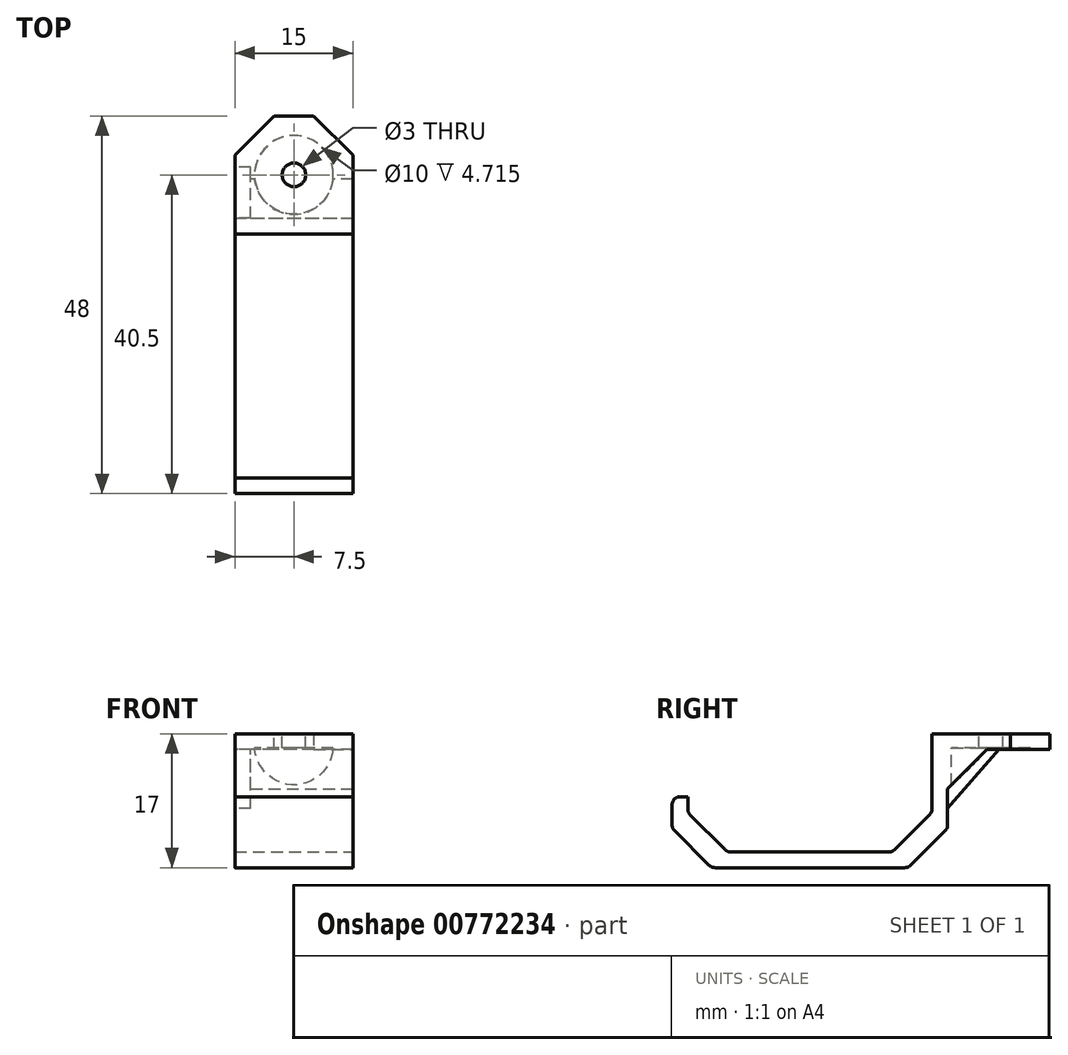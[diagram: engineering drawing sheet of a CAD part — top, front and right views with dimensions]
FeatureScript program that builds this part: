
annotation { "Feature Type Name" : "Feature", "Feature Type Description" : "" }
export const myFeature = defineFeature(function(context is Context, id is Id, definition is map)
    precondition{}
    {
        {
            var Q0;
            Q0=qCreatedBy(makeId("Right.planeOp"),FACE);
            var sketch = newSketch(context, id + "F0", { "sketchPlane" : qUnion([Q0])});
            skLineSegment(sketch, "E0", {"start": v(-35, 0) * mm, "end": v(0, 0) * mm});
            skLineSegment(sketch, "E1", {"start": v(0, 0) * mm, "end": v(0, 15) * mm});
            skLineSegment(sketch, "E2", {"start": v(0, 15) * mm, "end": v(13, 15) * mm});
            skLineSegment(sketch, "E3", {"start": v(13, 15) * mm, "end": v(13, 17) * mm});
            skLineSegment(sketch, "E4", {"start": v(13, 17) * mm, "end": v(-2, 17) * mm});
            skLineSegment(sketch, "E5", {"start": v(-2, 17) * mm, "end": v(-2, 2) * mm});
            skLineSegment(sketch, "E6", {"start": v(-2, 2) * mm, "end": v(-33, 2) * mm});
            skLineSegment(sketch, "E7", {"start": v(-33, 9) * mm, "end": v(-35, 9) * mm});
            skLineSegment(sketch, "E8", {"start": v(-35, 9) * mm, "end": v(-35, 0) * mm});
            skPoint(sketch, "E9", {"position": v(6.5, 15) * mm});
            skLineSegment(sketch, "E10", {"start": v(-33, 9) * mm, "end": v(-33, 2) * mm});
            skLineSegment(sketch, "E11", {"start": v(0, 7.5) * mm, "end": v(6.5, 15) * mm});
            skSolve(sketch);
        }
        {
            var Q0;
            {var subQ4=sQuery(id+"F0.wireOp",EDGE,"E0");Q0=makeQuery(id+"F0.imprint","IMPRINT",FACE,{"disambiguationData":[TD([[makeQuery(id+"F0.imprint","IMPRINT",EDGE,{"derivedFrom":subQ4}),1.0]])]});}
            extrude(context, id + "F1", {"entities" : qUnion([Q0]), "depth" : 15 * mm, "offsetDistance" : 25 * mm});
        }
        {
            var Q0;
            {var subQ3=sQuery(id+"F0.wireOp",EDGE,"E11");Q0=makeQuery(id+"F0.imprint","IMPRINT",FACE,{"disambiguationData":[TD([[makeQuery(id+"F0.imprint","IMPRINT",EDGE,{"derivedFrom":subQ3}),1.0]])]});}
            extrude(context, id + "F2", {"entities" : qUnion([Q0]), "operationType" : NewBodyOperationType.ADD, "depth" : 2 * mm, "offsetDistance" : 25 * mm});
        }
        {
            var Q0;
            Q0=makeQuery(id+"F1.opExtrude","SWEPT_FACE",FACE,{"disambiguationData":[OSD([sQuery(id+"F0.wireOp",EDGE,"E2")])]});
            var sketch = newSketch(context, id + "F3", { "sketchPlane" : qUnion([Q0])});
            skPoint(sketch, "E12", {"position": v(7.5, -5.5) * mm});
            skPoint(sketch, "E12.positionSnap0", {"position": v(0, -5.5) * mm});
            skPoint(sketch, "E12.positionSnap1", {"position": v(7.5, 2) * mm});
            skSolve(sketch);
        }
        {
            var Q0;
            Q0=sQuery(id+"F3.wireOp",VERTEX,"E12");
            var Q1;
            Q1=makeQuery(id+"F1.opExtrude","SWEPT_BODY",BODY,{"disambiguationData":[OSD([sQuery(id+"F0.wireOp",EDGE,"E0"),sQuery(id+"F0.wireOp",EDGE,"E1"),sQuery(id+"F0.wireOp",EDGE,"E2"),sQuery(id+"F0.wireOp",EDGE,"E3"),sQuery(id+"F0.wireOp",EDGE,"E4"),sQuery(id+"F0.wireOp",EDGE,"E5"),sQuery(id+"F0.wireOp",EDGE,"E6"),sQuery(id+"F0.wireOp",EDGE,"E7"),sQuery(id+"F0.wireOp",EDGE,"E8"),sQuery(id+"F0.wireOp",EDGE,"E10")])]});
            hole(context, id + "F4", {"style" : HoleStyle.C_BORE, "endStyle" : HoleEndStyle.BLIND, "holeDiameter" : 3 * mm, "cBoreDiameter" : 10 * mm, "cBoreDepth" : 0.2 * mm, "majorDiameter" : 5 * mm, "holeDepth" : 100 * mm, "isTappedThrough" : true, "tappedDepth" : 12 * mm, "tapClearance" : 3, "locations" : qUnion([Q0]), "scope" : qUnion([Q1]), "startStyle" : HoleStartStyle.PART});
        }
        {
            var Q0;
            Q0=makeQuery(id+"F1.opExtrude","SWEPT_EDGE",EDGE,{"disambiguationData":[OSD([sQuery(id+"F0.wireOp",EDGE,"E5"),sQuery(id+"F0.wireOp",EDGE,"E6")])]});
            var Q1;
            Q1=makeQuery(id+"F1.opExtrude","SWEPT_EDGE",EDGE,{"disambiguationData":[OSD([sQuery(id+"F0.wireOp",EDGE,"E6"),sQuery(id+"F0.wireOp",EDGE,"E10")])]});
            var Q2;
            Q2=makeQuery(id+"F1.opExtrude","SWEPT_EDGE",EDGE,{"disambiguationData":[OSD([sQuery(id+"F0.wireOp",EDGE,"E0"),sQuery(id+"F0.wireOp",EDGE,"E8")])]});
            var Q3;
            Q3=makeQuery(id+"F1.opExtrude","CAP_EDGE",EDGE,{"disambiguationData":[OSD([sQuery(id+"F0.wireOp",EDGE,"E3")])],"isStart":false});
            var Q4;
            Q4=makeQuery(id+"F1.opExtrude","CAP_EDGE",EDGE,{"disambiguationData":[OSD([sQuery(id+"F0.wireOp",EDGE,"E3")])],"isStart":true});
            var Q5;
            Q5=makeQuery(id+"F1.opExtrude","SWEPT_EDGE",EDGE,{"disambiguationData":[OSD([sQuery(id+"F0.wireOp",EDGE,"E1"),sQuery(id+"F0.wireOp",EDGE,"E2")])]});
            var Q6;
            Q6=makeQuery(id+"F1.opExtrude","SWEPT_EDGE",EDGE,{"disambiguationData":[OSD([sQuery(id+"F0.wireOp",EDGE,"E0"),sQuery(id+"F0.wireOp",EDGE,"E1")])]});
            chamfer(context, id + "F5", {"entities" : qUnion([Q0, Q1, Q2, Q3, Q4, Q5, Q6]), "width" : 5 * mm, "tangentPropagation" : true});
        }
        {
            var Q0;
            Q0=makeQuery(id+"F1.opExtrude","SWEPT_EDGE",EDGE,{"disambiguationData":[OSD([sQuery(id+"F0.wireOp",EDGE,"E7"),sQuery(id+"F0.wireOp",EDGE,"E8")])]});
            var Q1;
            {var subQ0=sQuery(id+"F0.wireOp",EDGE,"E10");Q1=makeQuery(id+"F5.opChamfer","BLEND_EDGE",EDGE,{"blendedFrom":[makeQuery(id+"F1.opExtrude","SWEPT_EDGE",EDGE,{"disambiguationData":[OSD([sQuery(id+"F0.wireOp",EDGE,"E6"),subQ0])]}),makeQuery(id+"F1.opExtrude","SWEPT_FACE",FACE,{"disambiguationData":[OSD([subQ0])]})],"blendedInto":[makeQuery(id+"F1.opExtrude","SWEPT_FACE",FACE,{"disambiguationData":[OSD([subQ0])]})]});}
            var Q2;
            {var subQ0=sQuery(id+"F0.wireOp",EDGE,"E6");Q2=makeQuery(id+"F5.opChamfer","BLEND_EDGE",EDGE,{"blendedFrom":[makeQuery(id+"F1.opExtrude","SWEPT_EDGE",EDGE,{"disambiguationData":[OSD([subQ0,sQuery(id+"F0.wireOp",EDGE,"E10")])]}),makeQuery(id+"F1.opExtrude","SWEPT_FACE",FACE,{"disambiguationData":[OSD([subQ0])]})],"blendedInto":[makeQuery(id+"F1.opExtrude","SWEPT_FACE",FACE,{"disambiguationData":[OSD([subQ0])]})]});}
            var Q3;
            {var subQ0=sQuery(id+"F0.wireOp",EDGE,"E6");Q3=makeQuery(id+"F5.opChamfer","BLEND_EDGE",EDGE,{"blendedFrom":[makeQuery(id+"F1.opExtrude","SWEPT_EDGE",EDGE,{"disambiguationData":[OSD([sQuery(id+"F0.wireOp",EDGE,"E5"),subQ0])]}),makeQuery(id+"F1.opExtrude","SWEPT_FACE",FACE,{"disambiguationData":[OSD([subQ0])]})],"blendedInto":[makeQuery(id+"F1.opExtrude","SWEPT_FACE",FACE,{"disambiguationData":[OSD([subQ0])]})]});}
            var Q4;
            {var subQ0=sQuery(id+"F0.wireOp",EDGE,"E5");Q4=makeQuery(id+"F5.opChamfer","BLEND_EDGE",EDGE,{"blendedFrom":[makeQuery(id+"F1.opExtrude","SWEPT_EDGE",EDGE,{"disambiguationData":[OSD([subQ0,sQuery(id+"F0.wireOp",EDGE,"E6")])]}),makeQuery(id+"F1.opExtrude","SWEPT_FACE",FACE,{"disambiguationData":[OSD([subQ0])]})],"blendedInto":[makeQuery(id+"F1.opExtrude","SWEPT_FACE",FACE,{"disambiguationData":[OSD([subQ0])]})]});}
            var Q5;
            {var subQ0=sQuery(id+"F0.wireOp",EDGE,"E1");Q5=makeQuery(id+"F5.opChamfer","BLEND_EDGE",EDGE,{"blendedFrom":[makeQuery(id+"F1.opExtrude","SWEPT_EDGE",EDGE,{"disambiguationData":[OSD([sQuery(id+"F0.wireOp",EDGE,"E0"),subQ0])]}),makeQuery(id+"F1.opExtrude","SWEPT_FACE",FACE,{"disambiguationData":[OSD([subQ0])]})],"blendedInto":[makeQuery(id+"F1.opExtrude","SWEPT_FACE",FACE,{"disambiguationData":[OSD([subQ0])]})]});}
            var Q6;
            {var subQ0=sQuery(id+"F0.wireOp",EDGE,"E0");Q6=makeQuery(id+"F5.opChamfer","BLEND_EDGE",EDGE,{"blendedFrom":[makeQuery(id+"F1.opExtrude","SWEPT_EDGE",EDGE,{"disambiguationData":[OSD([subQ0,sQuery(id+"F0.wireOp",EDGE,"E1")])]}),makeQuery(id+"F1.opExtrude","SWEPT_FACE",FACE,{"disambiguationData":[OSD([subQ0])]})],"blendedInto":[makeQuery(id+"F1.opExtrude","SWEPT_FACE",FACE,{"disambiguationData":[OSD([subQ0])]})]});}
            var Q7;
            {var subQ0=sQuery(id+"F0.wireOp",EDGE,"E0");Q7=makeQuery(id+"F5.opChamfer","BLEND_EDGE",EDGE,{"blendedFrom":[makeQuery(id+"F1.opExtrude","SWEPT_EDGE",EDGE,{"disambiguationData":[OSD([subQ0,sQuery(id+"F0.wireOp",EDGE,"E8")])]}),makeQuery(id+"F1.opExtrude","SWEPT_FACE",FACE,{"disambiguationData":[OSD([subQ0])]})],"blendedInto":[makeQuery(id+"F1.opExtrude","SWEPT_FACE",FACE,{"disambiguationData":[OSD([subQ0])]})]});}
            var Q8;
            {var subQ0=sQuery(id+"F0.wireOp",EDGE,"E8");Q8=makeQuery(id+"F5.opChamfer","BLEND_EDGE",EDGE,{"blendedFrom":[makeQuery(id+"F1.opExtrude","SWEPT_EDGE",EDGE,{"disambiguationData":[OSD([sQuery(id+"F0.wireOp",EDGE,"E0"),subQ0])]}),makeQuery(id+"F1.opExtrude","SWEPT_FACE",FACE,{"disambiguationData":[OSD([subQ0])]})],"blendedInto":[makeQuery(id+"F1.opExtrude","SWEPT_FACE",FACE,{"disambiguationData":[OSD([subQ0])]})]});}
            fillet(context, id + "F6", {"entities" : qUnion([Q0, Q1, Q2, Q3, Q4, Q5, Q6, Q7, Q8]), "radius" : 1 * mm, "tangentPropagation" : true, "allowEdgeOverflow" : false});
        }
    });
